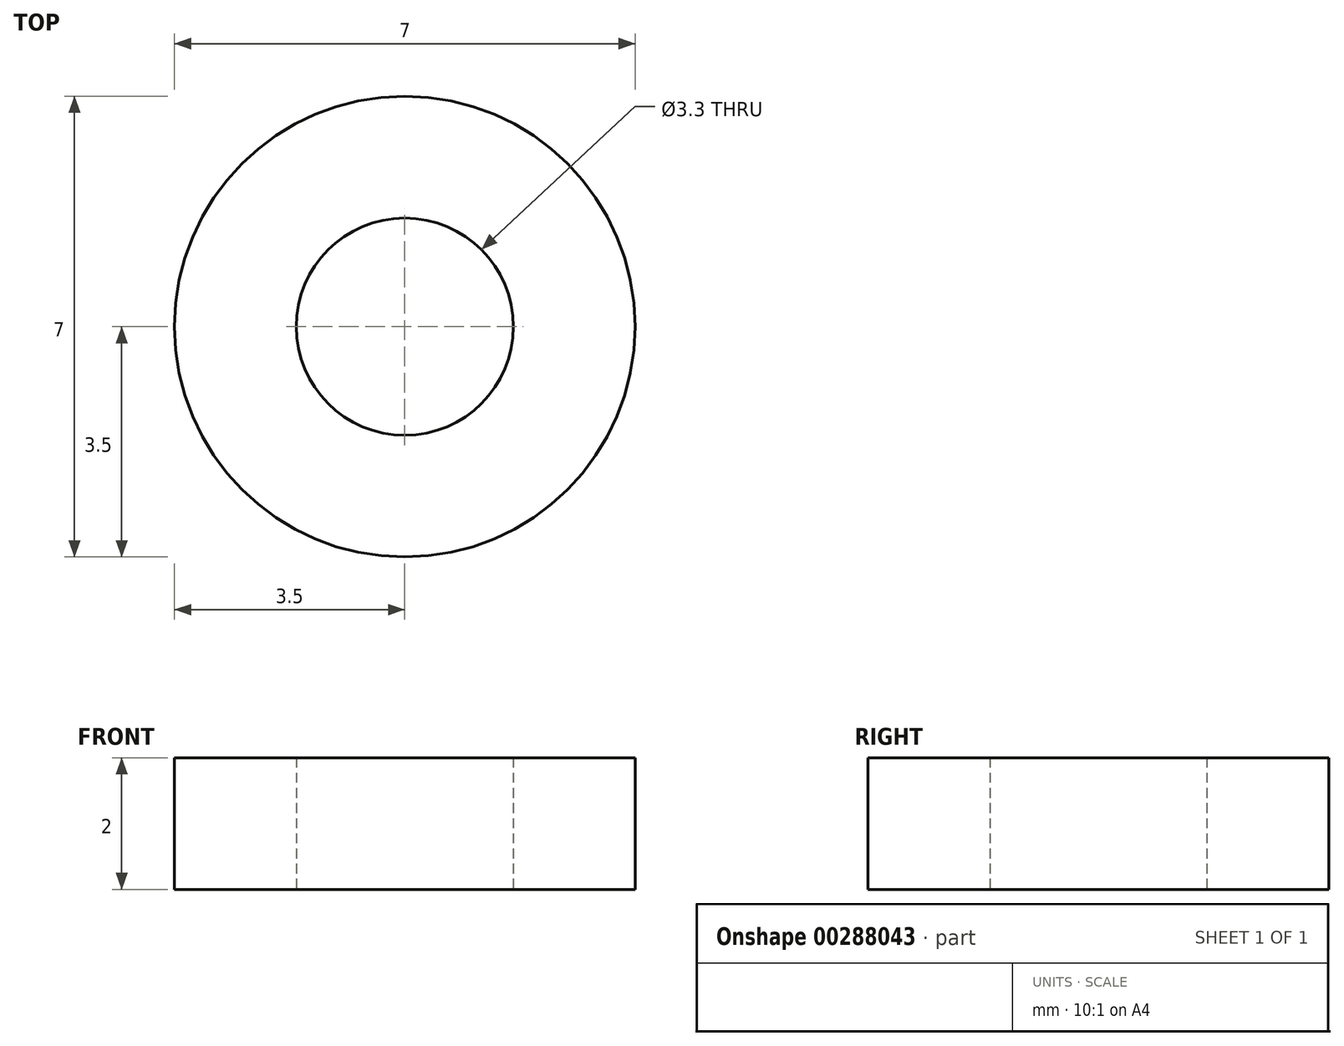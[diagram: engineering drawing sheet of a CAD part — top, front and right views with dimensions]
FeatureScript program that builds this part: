
annotation { "Feature Type Name" : "Feature", "Feature Type Description" : "" }
export const myFeature = defineFeature(function(context is Context, id is Id, definition is map)
    precondition{}
    {
        {
            var Q0;
            Q0=qCreatedBy(makeId("Top.planeOp"),FACE);
            var sketch = newSketch(context, id + "F0", { "sketchPlane" : qUnion([Q0])});
            skCircle(sketch, "E0", {"center": v(0, 0) * mm, "radius": 3.5 * mm});
            skCircle(sketch, "E1", {"center": v(0, 0) * mm, "radius": 1.65 * mm});
            skSolve(sketch);
        }
        {
            var Q0;
            Q0=makeQuery(id+"F0.imprint","IMPRINT",FACE,{"disambiguationData":[TD([[makeQuery(id+"F0.imprint","IMPRINT",EDGE,{"derivedFrom":sQuery(id+"F0.wireOp",EDGE,"E0")}),1.0]])]});
            extrude(context, id + "F1", {"entities" : qUnion([Q0]), "depth" : 2 * mm});
        }
    });
